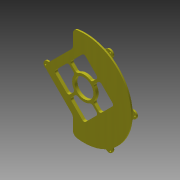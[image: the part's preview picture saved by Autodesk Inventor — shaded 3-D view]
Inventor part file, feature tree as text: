
AUTODESK INVENTOR PART (.ipt)
format: ipt  version: 2015 (Build 190159000, 159)  size: 351,744 bytes
history: native  units: mm
features: extrude x5, fillet x5, sketch x4, other x1
ambient origin geometry x8: Origin, YZ Plane, XZ Plane, XY Plane, X Axis, Y Axis, Z Axis, Center Point
bodies: Body1 (feature_tree)
feature tree (15):
  other  "Sólido1"
  extrude  "Extrusión1"  Depth=3.0mm TaperAngle=0.0deg
  extrude  "Extrusión2"  Depth=3.0mm
  fillet  "Empalme1"  Radius=3.0mm
  fillet  "Empalme2"  Radius=60.0mm
  extrude  "Extrusión3"  Depth=3.0mm
  fillet  "Empalme3"  Radius=8.0mm
  fillet  "Empalme4"  Radius=4.0mm
  sketch  "Boceto5"  dims[d16=3.0mm d17=0.0mm d18=3.0mm d19=3.0mm d21=40.0mm d22=20.0mm d23=20.0mm d24=5.0mm d25=360.0deg d26=5.0mm d27=5.0mm d28=5.0mm d29=10.0mm d30=2.451216mm d31=270.0mm d32=3.0mm d33=3.0mm d34=0.0mm d35=6.0mm d36=0.0mm d37=3.0mm]
  extrude  "Extrusión4"  Depth=3.0mm
  extrude  "Extrusión5"  Depth=3.0mm
  fillet  "Empalme5"  Radius=3.0mm
  sketch  "Boceto1"  dims[d0=10.0mm d1=10.0mm d2=3.0mm d3=0.0mm]
  sketch  "Boceto2"  dims[d4=4.0mm d5=8.0mm d6=3.0mm d7=0.0mm d8=60.0mm d10=360.0deg]
  sketch  "Boceto4"  dims[d12=3.0mm d13=3.0mm d14=8.0mm d15=4.0mm]
